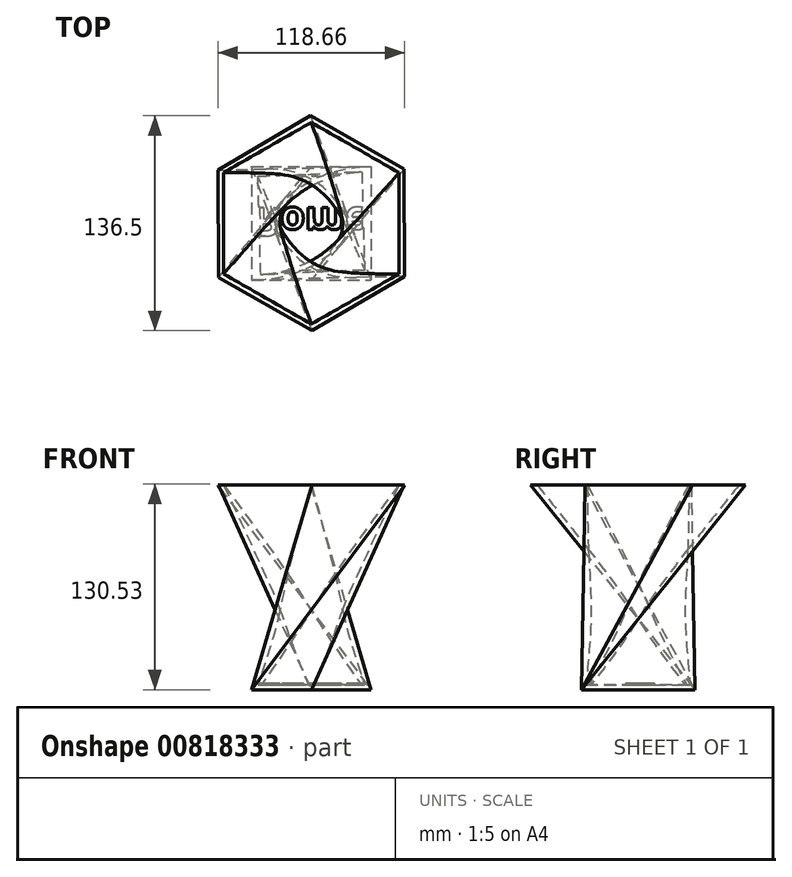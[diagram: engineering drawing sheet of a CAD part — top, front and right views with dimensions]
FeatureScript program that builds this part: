
annotation { "Feature Type Name" : "Feature", "Feature Type Description" : "" }
export const myFeature = defineFeature(function(context is Context, id is Id, definition is map)
    precondition{}
    {
        {
            var Q0;
            Q0=qCreatedBy(makeId("Top.planeOp"),FACE);
            cPlane(context, id + "F0", {"entities" : qUnion([Q0]), "cplaneType" : CPlaneType.OFFSET, "offset" : 130 * mm, "width" : 150 * mm, "height" : 150 * mm});
        }
        {
            var Q0;
            Q0=qCreatedBy(makeId("Top.planeOp"),FACE);
            var sketch = newSketch(context, id + "F1", { "sketchPlane" : qUnion([Q0])});
            skLineSegment(sketch, "E0.bottom", {"start": v(-37.93, 36.07) * mm, "end": v(37.93, 36.07) * mm});
            skLineSegment(sketch, "E0.top", {"start": v(-37.93, -36.07) * mm, "end": v(37.93, -36.07) * mm});
            skLineSegment(sketch, "E0.left", {"start": v(-37.93, 36.07) * mm, "end": v(-37.93, -36.07) * mm});
            skLineSegment(sketch, "E0.right", {"start": v(37.93, 36.07) * mm, "end": v(37.93, -36.07) * mm});
            skPoint(sketch, "E0.middle", {"position": v(0, 0) * mm});
            skSolve(sketch);
        }
        {
            var Q0;
            Q0=qCreatedBy(id+"F0.planeOp",FACE);
            var sketch = newSketch(context, id + "F2", { "sketchPlane" : qUnion([Q0])});
            skCircle(sketch, "E1.cCircle", {"center": v(0, 0) * mm, "radius": 59.11 * mm, "construction": true});
            skLineSegment(sketch, "E1.0", {"start": v(59.33, -33.75) * mm, "end": v(0.44, -68.25) * mm});
            skLineSegment(sketch, "E1.1", {"start": v(0.44, -68.25) * mm, "end": v(-58.89, -34.5) * mm});
            skLineSegment(sketch, "E1.2", {"start": v(-58.89, -34.5) * mm, "end": v(-59.33, 33.75) * mm});
            skLineSegment(sketch, "E1.3", {"start": v(-59.33, 33.75) * mm, "end": v(-0.44, 68.25) * mm});
            skLineSegment(sketch, "E1.4", {"start": v(-0.44, 68.25) * mm, "end": v(58.89, 34.5) * mm});
            skLineSegment(sketch, "E1.5", {"start": v(58.89, 34.5) * mm, "end": v(59.33, -33.75) * mm});
            skPoint(sketch, "E1.0.midPoint", {"position": v(29.89, -51) * mm});
            skSolve(sketch);
        }
        {
            var Q0;
            Q0=makeQuery(id+"F2.imprint","IMPRINT",FACE,{"disambiguationData":[TD([[makeQuery(id+"F2.imprint","IMPRINT",EDGE,{"derivedFrom":sQuery(id+"F2.wireOp",EDGE,"E1.0")}),-1.0]])]});
            var Q1;
            Q1=makeQuery(id+"F1.imprint","IMPRINT",FACE,{"disambiguationData":[TD([[makeQuery(id+"F1.imprint","IMPRINT",EDGE,{"derivedFrom":sQuery(id+"F1.wireOp",EDGE,"E0.bottom")}),-1.0]])]});
            var Q2;
            Q2=sQuery(id+"F1.wireOp",VERTEX,"E0.bottom.end");
            var Q3;
            Q3=sQuery(id+"F2.wireOp",VERTEX,"E1.2.end");
            loft(context, id + "F3", {"sheetProfilesArray" : [{ "sheetProfileEntities" : qUnion([Q0]) }, { "sheetProfileEntities" : qUnion([Q1]) }], "matchConnections" : true, "connections" : [{ "connectionEntities" : qUnion([Q2, Q3]), "connectionEdgeQueries" : qUnion([]), "connectionEdgeParameters" : [] }]});
        }
        {
            var Q0;
            Q0=makeQuery(id+"F3.opLoft","CAP_FACE",FACE,{"disambiguationData":[OSD([makeQuery(id+"F2.imprint","IMPRINT",FACE,{"disambiguationData":[TD([[makeQuery(id+"F2.imprint","IMPRINT",EDGE,{"derivedFrom":sQuery(id+"F2.wireOp",EDGE,"E1.0")}),-1.0]])]})])],"isStart":true});
            shell(context, id + "F4", {"entities" : qUnion([Q0]), "thickness" : 3 * mm});
        }
        {
            var Q0;
            Q0=makeQuery(id+"F3.opLoft","CAP_FACE",FACE,{"disambiguationData":[OSD([makeQuery(id+"F1.imprint","IMPRINT",FACE,{"disambiguationData":[TD([[makeQuery(id+"F1.imprint","IMPRINT",EDGE,{"derivedFrom":sQuery(id+"F1.wireOp",EDGE,"E0.bottom")}),-1.0]])]})])],"isStart":true});
            var sketch = newSketch(context, id + "F5", { "sketchPlane" : qUnion([Q0])});
            skText(sketch, "E2", { "text": "Rome\n", "fontName": "OpenSans-Bold.ttf"});
            const initialGuessF5  = {"E2": [-0.03658, -0.01009, 1, 0, 0.01838]};
            skSetInitialGuess(sketch, initialGuessF5);
            skSolve(sketch);
        }
        {
            var Q0;
            Q0 = qSketchRegion(id + "F5", true);
            extrude(context, id + "F6", {"entities" : qUnion([Q0]), "operationType" : NewBodyOperationType.ADD, "oppositeDirection" : true, "depth" : 4 * mm, "offsetDistance" : 25 * mm});
        }
    });
